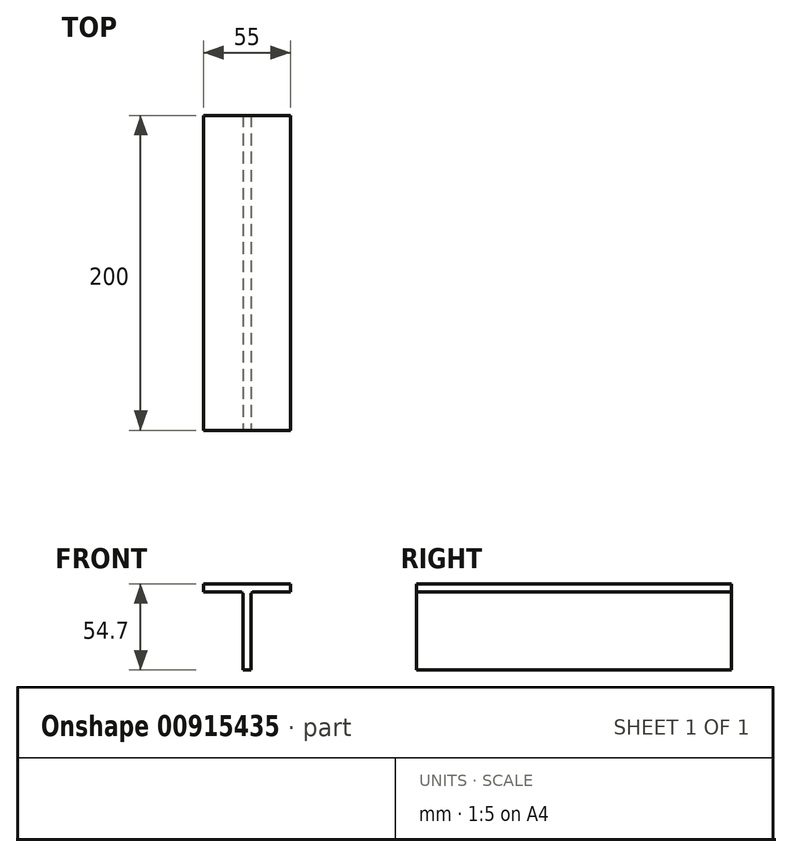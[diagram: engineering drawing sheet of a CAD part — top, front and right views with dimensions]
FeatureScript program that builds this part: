
annotation { "Feature Type Name" : "Feature", "Feature Type Description" : "" }
export const myFeature = defineFeature(function(context is Context, id is Id, definition is map)
    precondition{}
    {
        {
            var Q0;
            Q0=qCreatedBy(makeId("Front.planeOp"),FACE);
            var sketch = newSketch(context, id + "F0", { "sketchPlane" : qUnion([Q0])});
            skLineSegment(sketch, "E0", {"start": v(-30, 49.7) * mm, "end": v(-55, 49.7) * mm});
            skLineSegment(sketch, "E1", {"start": v(-55, 49.7) * mm, "end": v(-55, 54.7) * mm});
            skLineSegment(sketch, "E2", {"start": v(-55, 54.7) * mm, "end": v(0, 54.7) * mm});
            skLineSegment(sketch, "E3", {"start": v(-30, 49.7) * mm, "end": v(-30, 0) * mm});
            skLineSegment(sketch, "E4", {"start": v(-30, 0) * mm, "end": v(-25, 0) * mm});
            skLineSegment(sketch, "E5", {"start": v(-25, 0) * mm, "end": v(-25, 49.7) * mm});
            skLineSegment(sketch, "E6", {"start": v(-25, 49.7) * mm, "end": v(0, 49.7) * mm});
            skLineSegment(sketch, "E7", {"start": v(0, 54.7) * mm, "end": v(-55, 54.7) * mm});
            skLineSegment(sketch, "E8", {"start": v(0, 49.7) * mm, "end": v(0, 54.7) * mm});
            skSolve(sketch);
        }
        {
            var Q0;
            Q0 = qSketchRegion(id + "F0", true);
            extrude(context, id + "F1", {"entities" : qUnion([Q0]), "oppositeDirection" : true, "depth" : 200 * mm, "offsetDistance" : 25 * mm});
        }
        {
            var Q0;
            Q0=makeQuery(id+"F1.opExtrude","SWEPT_EDGE",EDGE,{"disambiguationData":[OSD([sQuery(id+"F0.wireOp",EDGE,"E0"),sQuery(id+"F0.wireOp",EDGE,"E3")])]});
            var Q1;
            Q1=makeQuery(id+"F1.opExtrude","SWEPT_EDGE",EDGE,{"disambiguationData":[OSD([sQuery(id+"F0.wireOp",EDGE,"E5"),sQuery(id+"F0.wireOp",EDGE,"E6")])]});
            fillet(context, id + "F2", {"entities" : qUnion([Q0, Q1]), "radius" : 2 * mm, "tangentPropagation" : true, "allowEdgeOverflow" : false});
        }
    });
